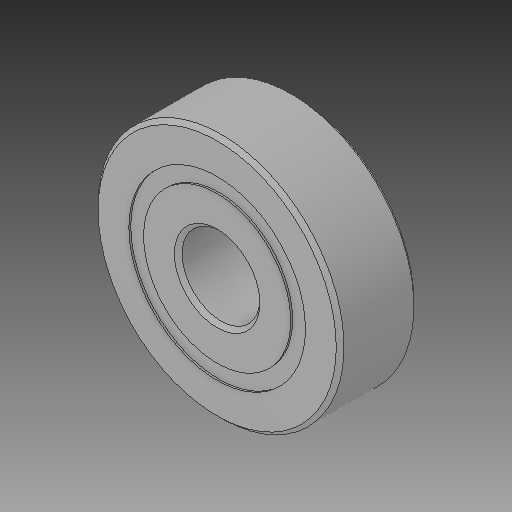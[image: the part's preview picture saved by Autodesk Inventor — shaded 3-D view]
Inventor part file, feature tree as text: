
AUTODESK INVENTOR PART (.ipt)
format: ipt  version: 2019 (Build 230136000, 136)  size: 726,016 bytes
history: imported  units: mm
features: imported_body x1
ambient origin geometry x8: Origin, YZ Plane, XZ Plane, XY Plane, X Axis, Y Axis, Z Axis, Center Point
bodies: Solide1 (imported_parasolid), Solide2 (imported_parasolid), Solide3 (imported_parasolid), Solide4 (imported_parasolid), Solide5 (imported_parasolid), Solide6 (imported_parasolid), Solide7 (imported_parasolid), Solide8 (imported_parasolid), Solide9 (imported_parasolid), Solide10 (imported_parasolid), Solide11 (imported_parasolid), Solide12 (imported_parasolid), Solide13 (imported_parasolid), Solide14 (imported_parasolid), Solide15 (imported_parasolid), Solide16 (imported_parasolid), Solide17 (imported_parasolid), Solide18 (imported_parasolid), Body1 (imported_parasolid), Body2 (imported_parasolid), Body3 (imported_parasolid), Body4 (imported_parasolid), Body5 (imported_parasolid), Body6 (imported_parasolid), Body7 (imported_parasolid), Body8 (imported_parasolid), Body9 (imported_parasolid), Body10 (imported_parasolid), Body11 (imported_parasolid), Body12 (imported_parasolid), Body13 (imported_parasolid), Body14 (imported_parasolid), Body15 (imported_parasolid), Body16 (imported_parasolid), Body17 (imported_parasolid), Body18 (imported_parasolid)
feature tree (1):
  imported_body  NMx_Import_Brep_tag  [imported B-rep: ~38 faces, bbox_mm=[18.7, 0.0, 6.0]]
